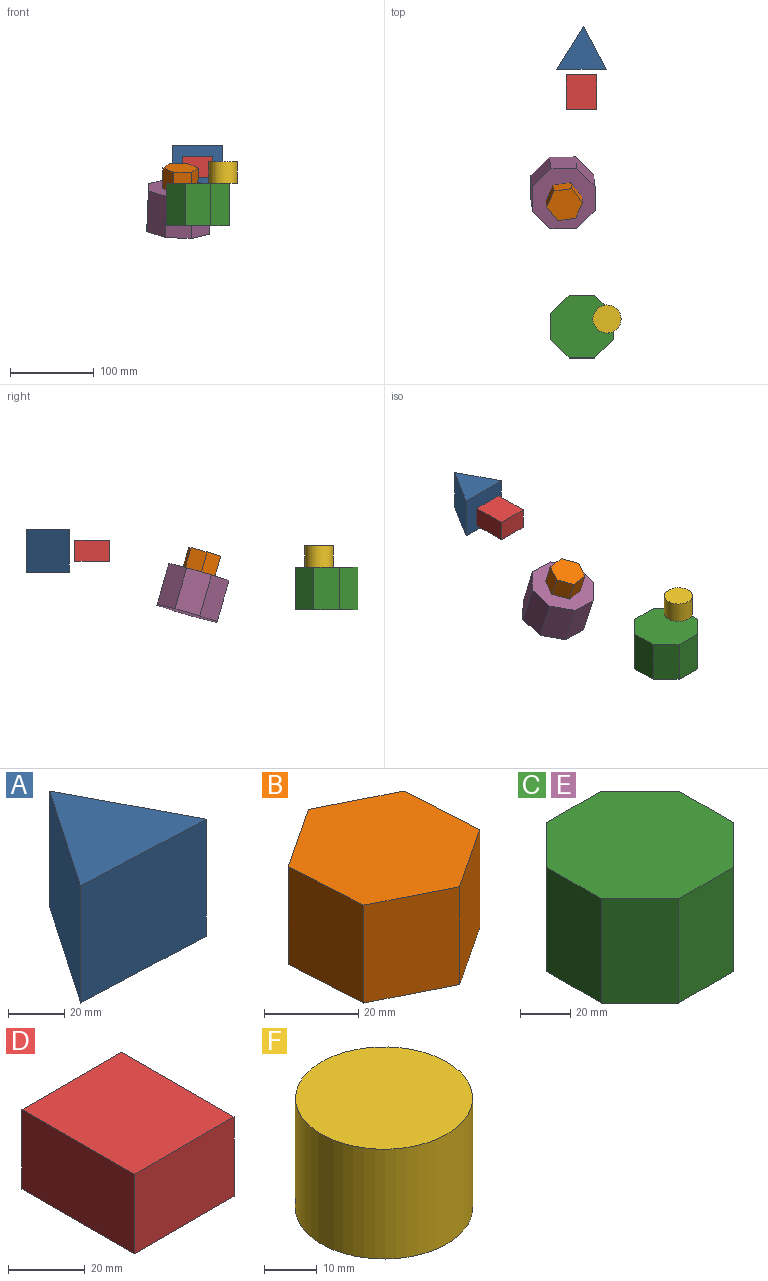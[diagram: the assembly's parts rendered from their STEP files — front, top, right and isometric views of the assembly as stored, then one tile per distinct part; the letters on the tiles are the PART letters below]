
ASSEMBLY  parts=6 mates=3
PART A: 5 faces, bbox 60.5x51.5x50.8 mm
  f0: plane 50.8x49.02mm, normal (-0.83,0.56,0), area 3018mm2, adj f1,f2,f3,f4
  f1: plane 60.52x50.8mm, normal (-0.04,-1,0), area 3077.1mm2, adj f0,f2,f3,f4
  f2: plane 51.47x50.8mm, normal (0.89,0.46,0), area 2951.8mm2, adj f0,f1,f3,f4
  f3: plane 60.52x51.47mm, normal (0,0,1), area 1524.6mm2, adj f0,f1,f2
  f4: plane 60.52x51.47mm, normal (0,0,-1), area 1524.6mm2, adj f0,f1,f2
PART B: 8 faces, bbox 38.3x42.7x25.4 mm
  f0: plane 25.4x19.15mm, normal (-0.45,-0.89,0), area 543.5mm2, adj f1,f5,f6,f7
  f1: plane 25.4x17.85mm, normal (0.55,-0.83,0), area 543.5mm2, adj f0,f2,f6,f7
  f2: plane 25.4x21.36mm, normal (1,0.06,0), area 543.5mm2, adj f1,f3,f6,f7
  f3: plane 25.4x19.15mm, normal (0.45,0.89,0), area 543.5mm2, adj f2,f4,f6,f7
  f4: plane 25.4x17.85mm, normal (-0.55,0.83,0), area 543.5mm2, adj f3,f5,f6,f7
  f5: plane 25.4x21.36mm, normal (-1,-0.06,0), area 543.5mm2, adj f0,f4,f6,f7
  f6: plane 42.72x38.29mm, normal (0,0,1), area 1189.7mm2, adj f0,f1,f2,f3,f4,f5
  f7: plane 42.72x38.29mm, normal (0,0,-1), area 1189.7mm2, adj f0,f1,f2,f3,f4,f5
PART C: 10 faces, bbox 74.4x74.4x50.8 mm
  f0: plane 50.8x21.8mm, normal (0.71,-0.71,0), area 1566mm2, adj f1,f7,f8,f9
  f1: plane 50.8x30.83mm, normal (1,0,0), area 1566mm2, adj f0,f2,f8,f9
  f2: plane 50.8x21.8mm, normal (0.71,0.71,0), area 1566mm2, adj f1,f3,f8,f9
  f3: plane 50.8x30.83mm, normal (0,1,0), area 1566mm2, adj f2,f4,f8,f9
  f4: plane 50.8x21.8mm, normal (-0.71,0.71,0), area 1566mm2, adj f3,f5,f8,f9
  f5: plane 50.8x30.83mm, normal (-1,0,0), area 1566mm2, adj f4,f6,f8,f9
  f6: plane 50.8x21.8mm, normal (-0.71,-0.71,0), area 1566mm2, adj f5,f7,f8,f9
  f7: plane 50.8x30.83mm, normal (0,-1,0), area 1566mm2, adj f0,f6,f8,f9
  f8: plane 74.42x74.42mm, normal (0,0,1), area 4588.4mm2, adj f0,f1,f2,f3,f4,f5,f6,f7
  f9: plane 74.42x74.42mm, normal (0,0,-1), area 4588.4mm2, adj f0,f1,f2,f3,f4,f5,f6,f7
PART D: 6 faces, bbox 36.8x41.4x25.4 mm
  f0: plane 36.81x25.4mm, normal (0,-1,0), area 935mm2, adj f1,f3,f4,f5
  f1: plane 41.42x25.4mm, normal (1,0,0), area 1052.2mm2, adj f0,f2,f4,f5
  f2: plane 36.81x25.4mm, normal (0,1,0), area 935mm2, adj f1,f3,f4,f5
  f3: plane 41.42x25.4mm, normal (-1,0,0), area 1052.2mm2, adj f0,f2,f4,f5
  f4: plane 41.42x36.81mm, normal (0,0,1), area 1524.9mm2, adj f0,f1,f2,f3
  f5: plane 41.42x36.81mm, normal (0,0,-1), area 1524.9mm2, adj f0,f1,f2,f3
PART E: same geometry as C
PART F: 3 faces, bbox 33.5x33.5x25.4 mm
  f0: cylinder r=16.74mm len=33.48mm, axis (0,0,-1), area 2671.8mm2, adj f1,f2
  f1: plane 33.48x33.48mm, normal (0,0,1), area 880.5mm2, adj f0
  f2: plane 33.48x33.48mm, normal (0,0,-1), area 880.5mm2, adj f0
PLACE A rot(axis=(0.88,0.47,0),180deg) t=(-68.72,84.58,38.1)mm
PLACE B rot(axis=(0.05,-0.13,0.99),154.4deg) t=(-141.77,-63.65,-15.92)mm
PLACE C t=(-13.46,-239.71,-57.61)mm fixed
PLACE D t=(-51.2,82.98,0)mm fixed
PLACE E rot(axis=(0.99,0.14,0.02),16.2deg) t=(-37.05,-71.15,-75.26)mm fixed
PLACE F t=(-78.51,-250.15,-6.81)mm
MATE revolute E.f8 <-> B.f7  axis (0.04,-0.28,0.96) through (-72.23,-44.07,-13.14)mm
MATE slider A.f0 <-> D.f2  axis (0,-1,0) through (-51.2,110.51,12.7)mm
MATE planar C.f8 <-> F.f0  axis (0,0,1) through (-50.67,-196.53,-6.81)mm
